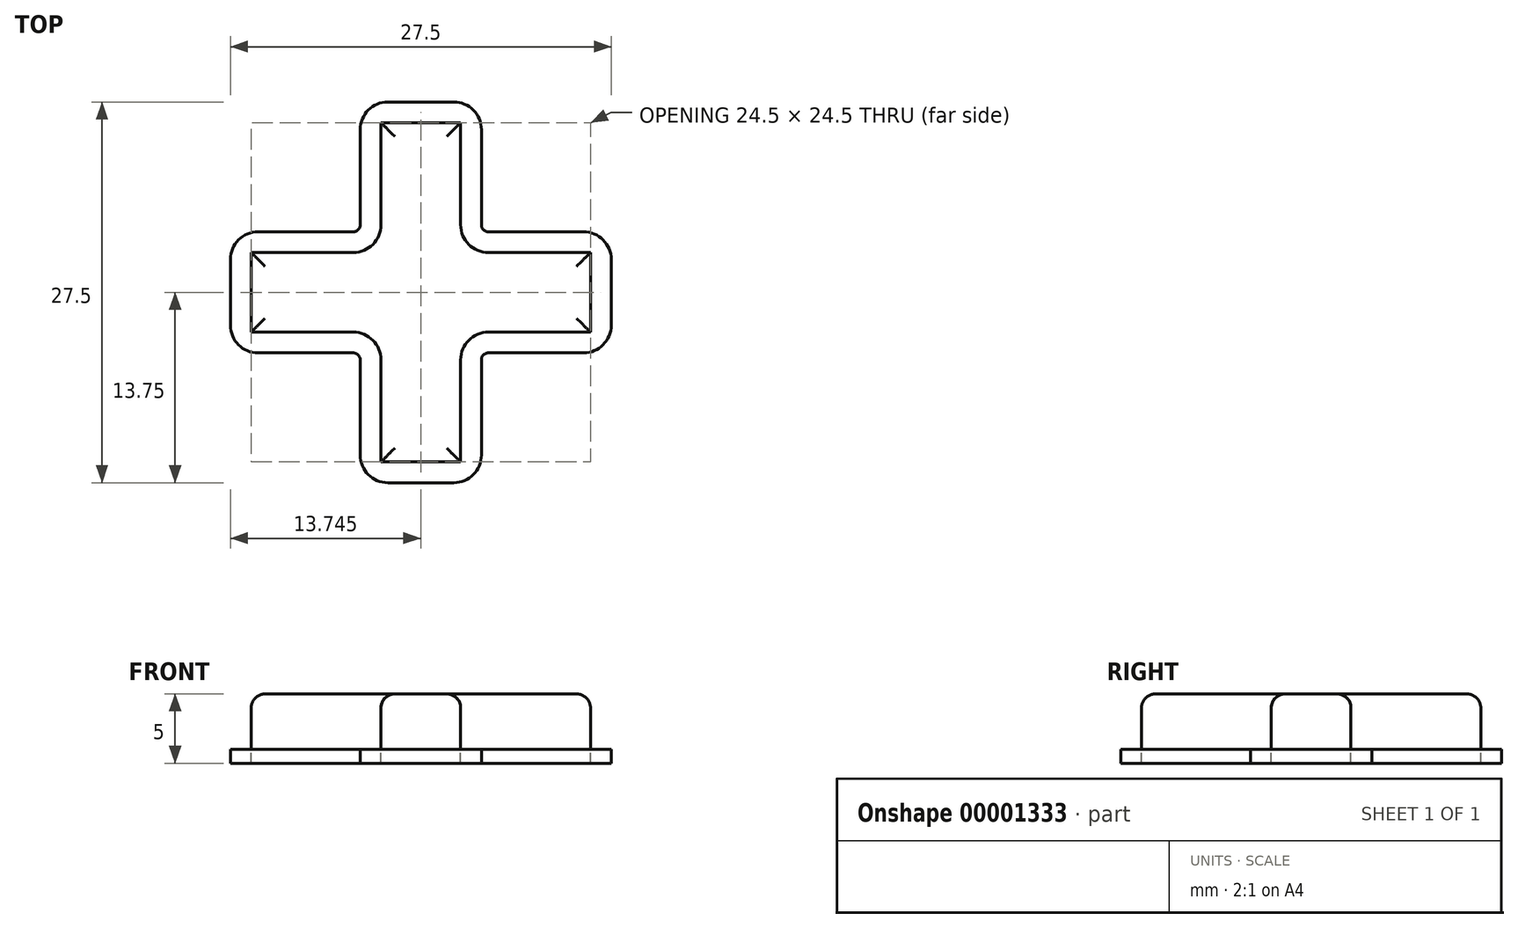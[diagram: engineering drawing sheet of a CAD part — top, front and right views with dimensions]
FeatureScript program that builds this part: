
annotation { "Feature Type Name" : "Feature", "Feature Type Description" : "" }
export const myFeature = defineFeature(function(context is Context, id is Id, definition is map)
    precondition{}
    {
        {
            var Q0;
            Q0=qCreatedBy(makeId("Top.planeOp"),FACE);
            var sketch = newSketch(context, id + "F0", { "sketchPlane" : qUnion([Q0])});
            skLineSegment(sketch, "E0", {"start": v(-5.75, 0) * mm, "end": v(0, 0) * mm});
            skLineSegment(sketch, "E1", {"start": v(0, 0) * mm, "end": v(0, -7.38) * mm});
            skLineSegment(sketch, "E2", {"start": v(2, -9.38) * mm, "end": v(9.38, -9.38) * mm});
            skLineSegment(sketch, "E3", {"start": v(9.38, -9.38) * mm, "end": v(9.38, -15.13) * mm});
            skLineSegment(sketch, "E4", {"start": v(9.38, -15.13) * mm, "end": v(2, -15.13) * mm});
            skLineSegment(sketch, "E5", {"start": v(0, -17.12) * mm, "end": v(0, -24.5) * mm});
            skLineSegment(sketch, "E6", {"start": v(0, -24.5) * mm, "end": v(-5.75, -24.5) * mm});
            skLineSegment(sketch, "E7", {"start": v(-5.75, -24.5) * mm, "end": v(-5.75, -17.12) * mm});
            skLineSegment(sketch, "E8", {"start": v(-7.75, -15.13) * mm, "end": v(-15.12, -15.13) * mm});
            skLineSegment(sketch, "E9", {"start": v(-15.12, -15.13) * mm, "end": v(-15.12, -9.38) * mm});
            skLineSegment(sketch, "E10", {"start": v(-15.12, -9.38) * mm, "end": v(-7.75, -9.38) * mm});
            skLineSegment(sketch, "E11", {"start": v(-5.75, -7.38) * mm, "end": v(-5.75, 0) * mm});
            skPoint(sketch, "E12.visualSharp", {"position": v(0, -15.13) * mm});
            skArc(sketch, "E12.filletArc", {"start": v(2, -15.12) * mm, "mid": v(0.59, -15.71) * mm, "end": v(0, -17.12) * mm});
            skPoint(sketch, "E13.visualSharp", {"position": v(-5.75, -15.13) * mm});
            skArc(sketch, "E13.filletArc", {"start": v(-5.75, -17.12) * mm, "mid": v(-6.34, -15.71) * mm, "end": v(-7.75, -15.12) * mm});
            skPoint(sketch, "E14.visualSharp", {"position": v(-5.75, -9.38) * mm});
            skArc(sketch, "E14.filletArc", {"start": v(-7.75, -9.38) * mm, "mid": v(-6.34, -8.79) * mm, "end": v(-5.75, -7.38) * mm});
            skPoint(sketch, "E15.visualSharp", {"position": v(0, -9.38) * mm});
            skArc(sketch, "E15.filletArc", {"start": v(0, -7.38) * mm, "mid": v(0.59, -8.79) * mm, "end": v(2, -9.38) * mm});
            skLineSegment(sketch, "E16.0", {"start": v(-7.25, -26) * mm, "end": v(-7.25, -17.12) * mm});
            skLineSegment(sketch, "E16.1", {"start": v(1.5, -26) * mm, "end": v(-7.25, -26) * mm});
            skLineSegment(sketch, "E16.2", {"start": v(1.5, -17.12) * mm, "end": v(1.5, -26) * mm});
            skArc(sketch, "E16.3", {"start": v(2, -16.62) * mm, "mid": v(1.65, -16.77) * mm, "end": v(1.5, -17.12) * mm});
            skLineSegment(sketch, "E16.4", {"start": v(10.88, -16.63) * mm, "end": v(2, -16.63) * mm});
            skArc(sketch, "E16.5", {"start": v(-7.25, -17.12) * mm, "mid": v(-7.4, -16.77) * mm, "end": v(-7.75, -16.62) * mm});
            skLineSegment(sketch, "E16.6", {"start": v(10.88, -7.88) * mm, "end": v(10.88, -16.63) * mm});
            skLineSegment(sketch, "E16.7", {"start": v(2, -7.88) * mm, "end": v(10.88, -7.88) * mm});
            skArc(sketch, "E16.8", {"start": v(1.5, -7.38) * mm, "mid": v(1.65, -7.73) * mm, "end": v(2, -7.88) * mm});
            skLineSegment(sketch, "E16.9", {"start": v(1.5, 1.5) * mm, "end": v(1.5, -7.38) * mm});
            skLineSegment(sketch, "E16.10", {"start": v(-7.25, 1.5) * mm, "end": v(1.5, 1.5) * mm});
            skLineSegment(sketch, "E16.11", {"start": v(-7.25, -7.38) * mm, "end": v(-7.25, 1.5) * mm});
            skArc(sketch, "E16.12", {"start": v(-7.75, -7.88) * mm, "mid": v(-7.4, -7.73) * mm, "end": v(-7.25, -7.38) * mm});
            skLineSegment(sketch, "E16.13", {"start": v(-16.62, -7.88) * mm, "end": v(-7.75, -7.88) * mm});
            skLineSegment(sketch, "E16.14", {"start": v(-16.62, -16.63) * mm, "end": v(-16.62, -7.88) * mm});
            skLineSegment(sketch, "E16.15", {"start": v(-7.75, -16.63) * mm, "end": v(-16.62, -16.63) * mm});
            skSolve(sketch);
        }
        {
            var Q0;
            Q0=makeQuery(id+"F0.imprint","IMPRINT",FACE,{"disambiguationData":[TD([[makeQuery(id+"F0.imprint","IMPRINT",EDGE,{"derivedFrom":sQuery(id+"F0.wireOp",EDGE,"E0")}),-1.0]])]});
            extrude(context, id + "F1", {"entities" : qUnion([Q0]), "depth" : 4 * mm});
        }
        {
            var Q0;
            Q0=makeQuery(id+"F0.imprint","IMPRINT",FACE,{"disambiguationData":[TD([[makeQuery(id+"F0.imprint","IMPRINT",EDGE,{"derivedFrom":sQuery(id+"F0.wireOp",EDGE,"E0")}),1.0]])]});
            extrude(context, id + "F2", {"entities" : qUnion([Q0]), "operationType" : NewBodyOperationType.ADD, "oppositeDirection" : true, "depth" : 1 * mm});
        }
        {
            var Q0;
            Q0=makeQuery(id+"F1.opExtrude","CAP_FACE",FACE,{"disambiguationData":[OSD([sQuery(id+"F0.wireOp",EDGE,"E0"),sQuery(id+"F0.wireOp",EDGE,"E1"),sQuery(id+"F0.wireOp",EDGE,"E2"),sQuery(id+"F0.wireOp",EDGE,"E3"),sQuery(id+"F0.wireOp",EDGE,"E4"),sQuery(id+"F0.wireOp",EDGE,"E5"),sQuery(id+"F0.wireOp",EDGE,"E6"),sQuery(id+"F0.wireOp",EDGE,"E7"),sQuery(id+"F0.wireOp",EDGE,"E8"),sQuery(id+"F0.wireOp",EDGE,"E9"),sQuery(id+"F0.wireOp",EDGE,"E10"),sQuery(id+"F0.wireOp",EDGE,"E11"),sQuery(id+"F0.wireOp",EDGE,"E12.filletArc"),sQuery(id+"F0.wireOp",EDGE,"E13.filletArc"),sQuery(id+"F0.wireOp",EDGE,"E14.filletArc"),sQuery(id+"F0.wireOp",EDGE,"E15.filletArc")])],"isStart":true});
            extrude(context, id + "F3", {"entities" : qUnion([Q0]), "depth" : 1 * mm});
        }
        {
            var Q0;
            Q0=makeQuery(id+"F1.opExtrude","CAP_EDGE",EDGE,{"disambiguationData":[OSD([sQuery(id+"F0.wireOp",EDGE,"E15.filletArc")])],"isStart":false});
            var Q1;
            Q1=makeQuery(id+"F1.opExtrude","CAP_EDGE",EDGE,{"disambiguationData":[OSD([sQuery(id+"F0.wireOp",EDGE,"E3")])],"isStart":false});
            var Q2;
            Q2=makeQuery(id+"F1.opExtrude","CAP_EDGE",EDGE,{"disambiguationData":[OSD([sQuery(id+"F0.wireOp",EDGE,"E4")])],"isStart":false});
            var Q3;
            Q3=makeQuery(id+"F1.opExtrude","CAP_EDGE",EDGE,{"disambiguationData":[OSD([sQuery(id+"F0.wireOp",EDGE,"E5")])],"isStart":false});
            var Q4;
            Q4=makeQuery(id+"F1.opExtrude","CAP_EDGE",EDGE,{"disambiguationData":[OSD([sQuery(id+"F0.wireOp",EDGE,"E6")])],"isStart":false});
            var Q5;
            Q5=makeQuery(id+"F1.opExtrude","CAP_EDGE",EDGE,{"disambiguationData":[OSD([sQuery(id+"F0.wireOp",EDGE,"E7")])],"isStart":false});
            var Q6;
            Q6=makeQuery(id+"F1.opExtrude","CAP_EDGE",EDGE,{"disambiguationData":[OSD([sQuery(id+"F0.wireOp",EDGE,"E8")])],"isStart":false});
            var Q7;
            Q7=makeQuery(id+"F1.opExtrude","CAP_EDGE",EDGE,{"disambiguationData":[OSD([sQuery(id+"F0.wireOp",EDGE,"E13.filletArc")])],"isStart":false});
            var Q8;
            Q8=makeQuery(id+"F1.opExtrude","CAP_EDGE",EDGE,{"disambiguationData":[OSD([sQuery(id+"F0.wireOp",EDGE,"E10")])],"isStart":false});
            var Q9;
            Q9=makeQuery(id+"F1.opExtrude","CAP_EDGE",EDGE,{"disambiguationData":[OSD([sQuery(id+"F0.wireOp",EDGE,"E2")])],"isStart":false});
            var Q10;
            Q10=makeQuery(id+"F1.opExtrude","CAP_EDGE",EDGE,{"disambiguationData":[OSD([sQuery(id+"F0.wireOp",EDGE,"E12.filletArc")])],"isStart":false});
            var Q11;
            Q11=makeQuery(id+"F1.opExtrude","CAP_EDGE",EDGE,{"disambiguationData":[OSD([sQuery(id+"F0.wireOp",EDGE,"E1")])],"isStart":false});
            var Q12;
            Q12=makeQuery(id+"F1.opExtrude","CAP_EDGE",EDGE,{"disambiguationData":[OSD([sQuery(id+"F0.wireOp",EDGE,"E0")])],"isStart":false});
            var Q13;
            Q13=makeQuery(id+"F1.opExtrude","CAP_EDGE",EDGE,{"disambiguationData":[OSD([sQuery(id+"F0.wireOp",EDGE,"E11")])],"isStart":false});
            var Q14;
            Q14=makeQuery(id+"F1.opExtrude","CAP_EDGE",EDGE,{"disambiguationData":[OSD([sQuery(id+"F0.wireOp",EDGE,"E14.filletArc")])],"isStart":false});
            var Q15;
            Q15=makeQuery(id+"F1.opExtrude","CAP_EDGE",EDGE,{"disambiguationData":[OSD([sQuery(id+"F0.wireOp",EDGE,"E9")])],"isStart":false});
            fillet(context, id + "F4", {"entities" : qUnion([Q0, Q1, Q2, Q3, Q4, Q5, Q6, Q7, Q8, Q9, Q10, Q11, Q12, Q13, Q14, Q15]), "radius" : 1 * mm, "tangentPropagation" : true, "allowEdgeOverflow" : false});
        }
        {
            var Q0;
            Q0=makeQuery(id+"F2.opExtrude","SWEPT_EDGE",EDGE,{"disambiguationData":[OSD([sQuery(id+"F0.wireOp",EDGE,"E16.1"),sQuery(id+"F0.wireOp",EDGE,"E16.2")])]});
            var Q1;
            Q1=makeQuery(id+"F2.opExtrude","SWEPT_EDGE",EDGE,{"disambiguationData":[OSD([sQuery(id+"F0.wireOp",EDGE,"E16.0"),sQuery(id+"F0.wireOp",EDGE,"E16.1")])]});
            var Q2;
            Q2=makeQuery(id+"F2.opExtrude","SWEPT_EDGE",EDGE,{"disambiguationData":[OSD([sQuery(id+"F0.wireOp",EDGE,"E16.14"),sQuery(id+"F0.wireOp",EDGE,"E16.15")])]});
            var Q3;
            {var subQ0=sQuery(id+"F0.wireOp",EDGE,"E16.0");var subQ1=sQuery(id+"F0.wireOp",EDGE,"E16.5");var subQ2=sQuery(id+"F0.wireOp",EDGE,"E16.15");Q3=qUnion([makeQuery(id+"F2.opExtrude","SWEPT_EDGE",EDGE,{"disambiguationData":[OSD([subQ0,subQ1])]}),makeQuery(id+"F2.opExtrude","SWEPT_EDGE",EDGE,{"disambiguationData":[OSD([sQuery(id+"F0.wireOp",EDGE,"E16.14"),subQ2])]}),makeQuery(id+"F2.opExtrude","SWEPT_EDGE",EDGE,{"disambiguationData":[OSD([subQ1,subQ2])]}),makeQuery(id+"F2.opExtrude","SWEPT_EDGE",EDGE,{"disambiguationData":[OSD([subQ0,sQuery(id+"F0.wireOp",EDGE,"E16.1")])]})]);}
            var Q4;
            Q4=makeQuery(id+"F2.opExtrude","SWEPT_EDGE",EDGE,{"disambiguationData":[OSD([sQuery(id+"F0.wireOp",EDGE,"E16.13"),sQuery(id+"F0.wireOp",EDGE,"E16.14")])]});
            var Q5;
            {var subQ0=sQuery(id+"F0.wireOp",EDGE,"E16.13");var subQ1=sQuery(id+"F0.wireOp",EDGE,"E16.11");var subQ2=sQuery(id+"F0.wireOp",EDGE,"E16.12");Q5=qUnion([makeQuery(id+"F2.opExtrude","SWEPT_EDGE",EDGE,{"disambiguationData":[OSD([subQ0,sQuery(id+"F0.wireOp",EDGE,"E16.14")])]}),makeQuery(id+"F2.opExtrude","SWEPT_EDGE",EDGE,{"disambiguationData":[OSD([subQ1,subQ2])]}),makeQuery(id+"F2.opExtrude","SWEPT_EDGE",EDGE,{"disambiguationData":[OSD([sQuery(id+"F0.wireOp",EDGE,"E16.10"),subQ1])]}),makeQuery(id+"F2.opExtrude","SWEPT_EDGE",EDGE,{"disambiguationData":[OSD([subQ2,subQ0])]})]);}
            var Q6;
            Q6=makeQuery(id+"F2.opExtrude","SWEPT_EDGE",EDGE,{"disambiguationData":[OSD([sQuery(id+"F0.wireOp",EDGE,"E16.10"),sQuery(id+"F0.wireOp",EDGE,"E16.11")])]});
            var Q7;
            Q7=makeQuery(id+"F2.opExtrude","SWEPT_EDGE",EDGE,{"disambiguationData":[OSD([sQuery(id+"F0.wireOp",EDGE,"E16.9"),sQuery(id+"F0.wireOp",EDGE,"E16.10")])]});
            var Q8;
            {var subQ0=sQuery(id+"F0.wireOp",EDGE,"E16.9");var subQ1=sQuery(id+"F0.wireOp",EDGE,"E16.7");var subQ2=sQuery(id+"F0.wireOp",EDGE,"E16.8");Q8=qUnion([makeQuery(id+"F2.opExtrude","SWEPT_EDGE",EDGE,{"disambiguationData":[OSD([subQ0,sQuery(id+"F0.wireOp",EDGE,"E16.10")])]}),makeQuery(id+"F2.opExtrude","SWEPT_EDGE",EDGE,{"disambiguationData":[OSD([sQuery(id+"F0.wireOp",EDGE,"E16.6"),subQ1])]}),makeQuery(id+"F2.opExtrude","SWEPT_EDGE",EDGE,{"disambiguationData":[OSD([subQ1,subQ2])]}),makeQuery(id+"F2.opExtrude","SWEPT_EDGE",EDGE,{"disambiguationData":[OSD([subQ2,subQ0])]})]);}
            var Q9;
            Q9=makeQuery(id+"F2.opExtrude","SWEPT_EDGE",EDGE,{"disambiguationData":[OSD([sQuery(id+"F0.wireOp",EDGE,"E16.6"),sQuery(id+"F0.wireOp",EDGE,"E16.7")])]});
            var Q10;
            Q10=makeQuery(id+"F2.opExtrude","SWEPT_EDGE",EDGE,{"disambiguationData":[OSD([sQuery(id+"F0.wireOp",EDGE,"E16.4"),sQuery(id+"F0.wireOp",EDGE,"E16.6")])]});
            var Q11;
            {var subQ0=sQuery(id+"F0.wireOp",EDGE,"E16.3");var subQ1=sQuery(id+"F0.wireOp",EDGE,"E16.4");var subQ2=sQuery(id+"F0.wireOp",EDGE,"E16.2");Q11=qUnion([makeQuery(id+"F2.opExtrude","SWEPT_EDGE",EDGE,{"disambiguationData":[OSD([subQ0,subQ1])]}),makeQuery(id+"F2.opExtrude","SWEPT_EDGE",EDGE,{"disambiguationData":[OSD([sQuery(id+"F0.wireOp",EDGE,"E16.1"),subQ2])]}),makeQuery(id+"F2.opExtrude","SWEPT_EDGE",EDGE,{"disambiguationData":[OSD([subQ2,subQ0])]}),makeQuery(id+"F2.opExtrude","SWEPT_EDGE",EDGE,{"disambiguationData":[OSD([subQ1,sQuery(id+"F0.wireOp",EDGE,"E16.6")])]})]);}
            fillet(context, id + "F5", {"entities" : qUnion([Q0, Q1, Q2, Q3, Q4, Q5, Q6, Q7, Q8, Q9, Q10, Q11]), "radius" : 2 * mm, "tangentPropagation" : true, "allowEdgeOverflow" : false});
        }
    });
